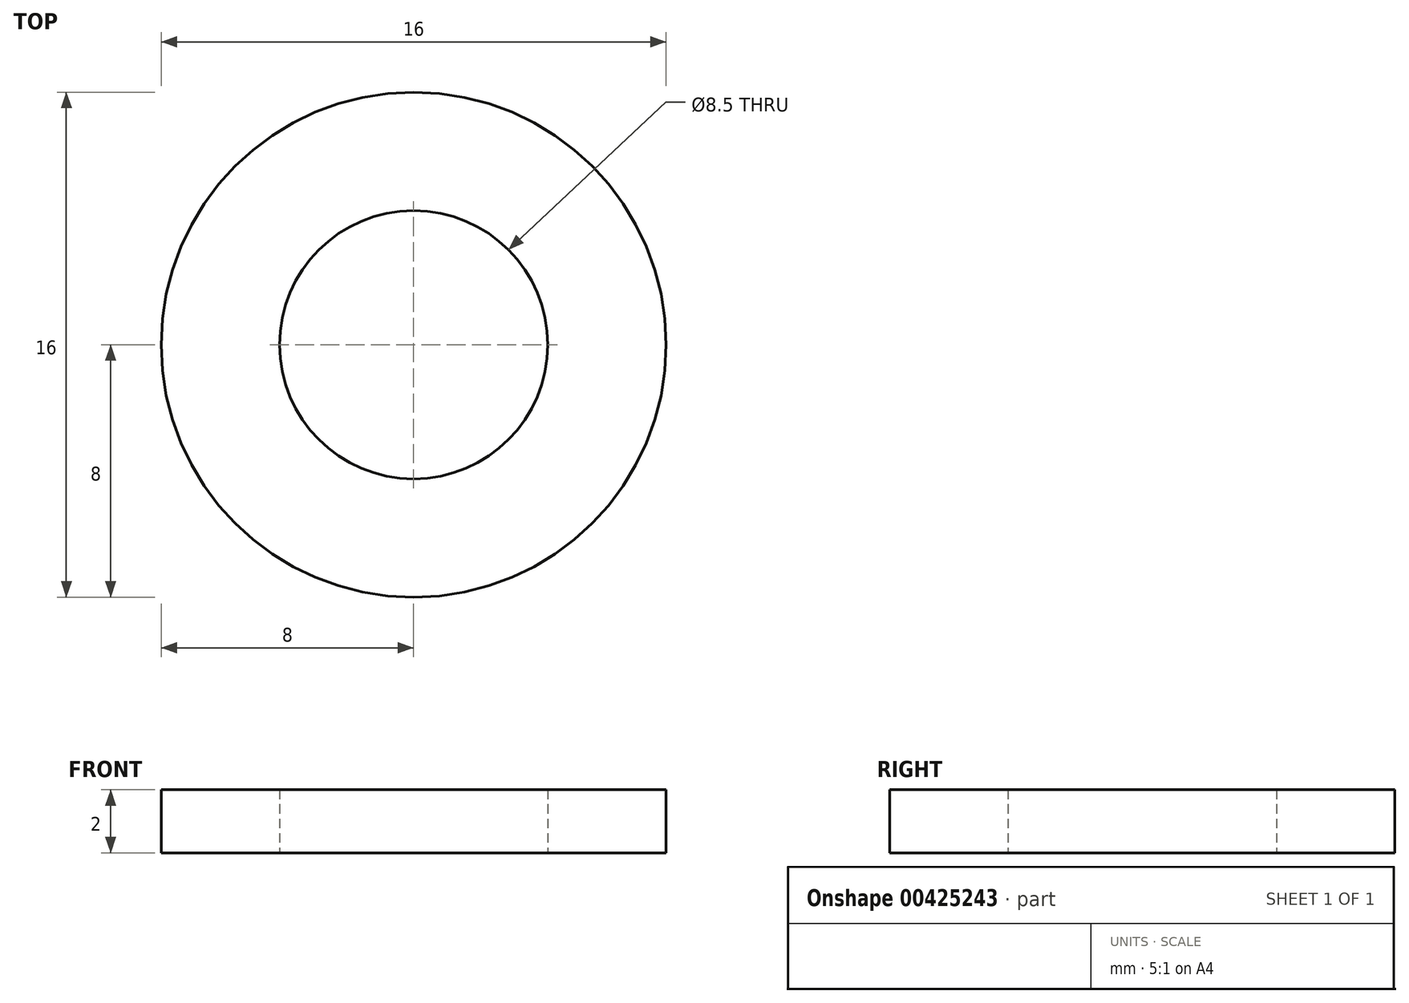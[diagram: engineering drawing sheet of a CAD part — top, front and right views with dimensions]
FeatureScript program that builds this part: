
annotation { "Feature Type Name" : "Feature", "Feature Type Description" : "" }
export const myFeature = defineFeature(function(context is Context, id is Id, definition is map)
    precondition{}
    {
        {
            var Q0;
            Q0=qCreatedBy(makeId("Top.planeOp"),FACE);
            var sketch = newSketch(context, id + "F0", { "sketchPlane" : qUnion([Q0])});
            skCircle(sketch, "E0", {"center": v(0, 0) * mm, "radius": 8 * mm});
            skCircle(sketch, "E1", {"center": v(0, 0) * mm, "radius": 4.25 * mm});
            skSolve(sketch);
        }
        {
            var Q0;
            Q0=makeQuery(id+"F0.imprint","IMPRINT",FACE,{"disambiguationData":[TD([[makeQuery(id+"F0.imprint","IMPRINT",EDGE,{"derivedFrom":sQuery(id+"F0.wireOp",EDGE,"E0")}),1.0]])]});
            extrude(context, id + "F1", {"entities" : qUnion([Q0]), "depth" : 2 * mm});
        }
    });
